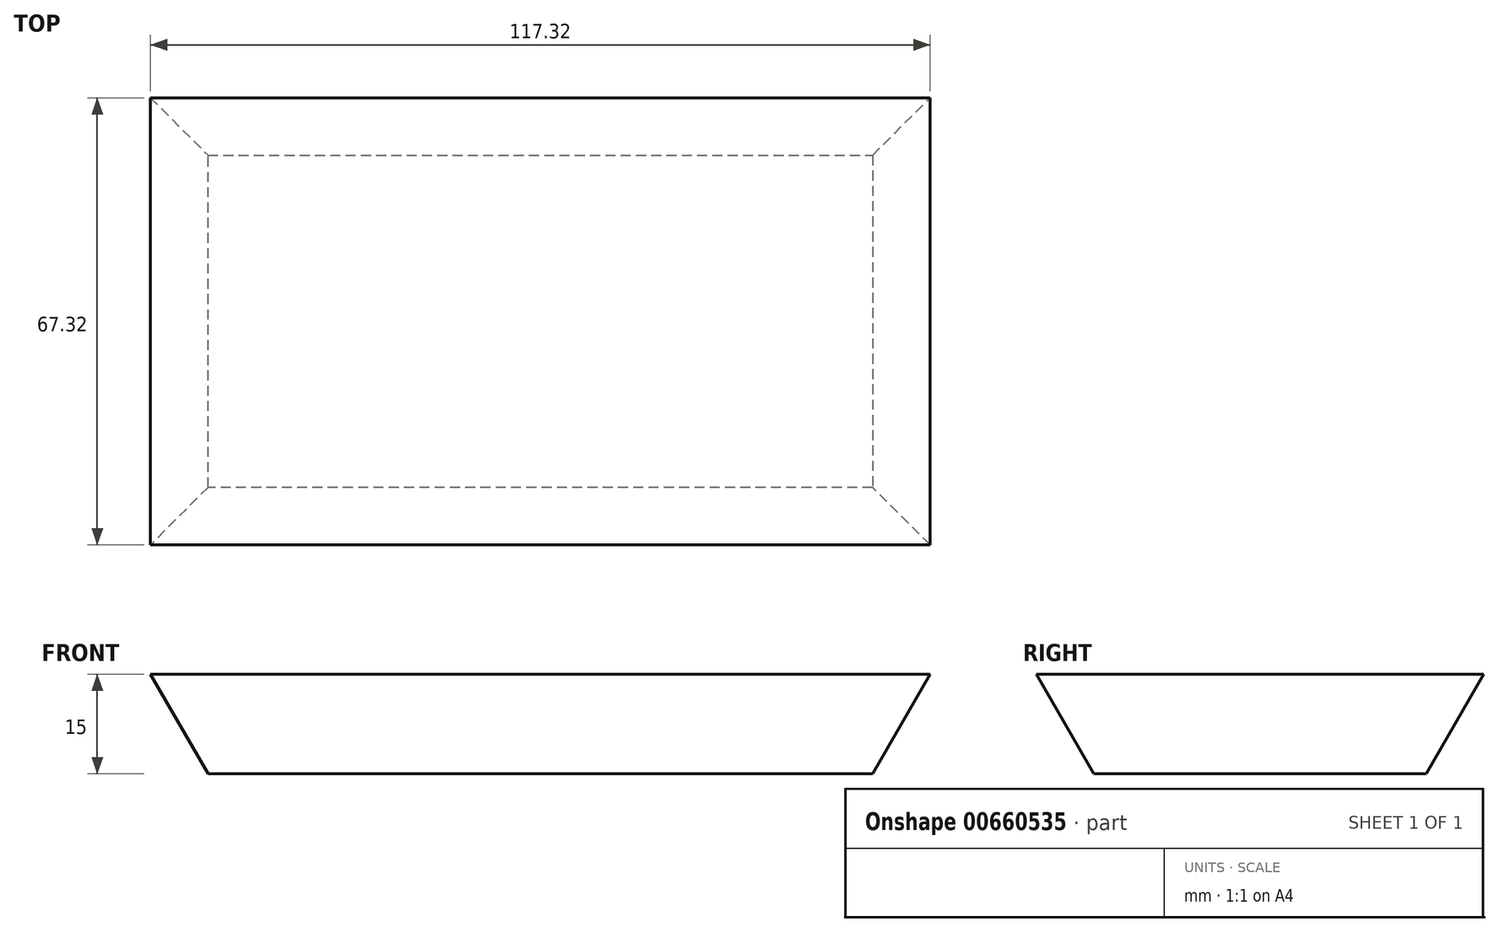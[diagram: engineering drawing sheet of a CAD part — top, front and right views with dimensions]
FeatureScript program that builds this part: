
annotation { "Feature Type Name" : "Feature", "Feature Type Description" : "" }
export const myFeature = defineFeature(function(context is Context, id is Id, definition is map)
    precondition{}
    {
        {
            var Q0;
            Q0=qCreatedBy(makeId("Top.planeOp"),FACE);
            var sketch = newSketch(context, id + "F0", { "sketchPlane" : qUnion([Q0])});
            skLineSegment(sketch, "E0.bottom", {"start": v(0, 0) * mm, "end": v(100, 0) * mm});
            skLineSegment(sketch, "E0.top", {"start": v(0, 50) * mm, "end": v(100, 50) * mm});
            skLineSegment(sketch, "E0.left", {"start": v(0, 0) * mm, "end": v(0, 50) * mm});
            skLineSegment(sketch, "E0.right", {"start": v(100, 0) * mm, "end": v(100, 50) * mm});
            skSolve(sketch);
        }
        {
            var Q0;
            Q0=makeQuery(id+"F0.imprint","IMPRINT",FACE,{"disambiguationData":[TD([[makeQuery(id+"F0.imprint","IMPRINT",EDGE,{"derivedFrom":sQuery(id+"F0.wireOp",EDGE,"E0.bottom")}),1.0]])]});
            extrude(context, id + "F1", {"entities" : qUnion([Q0]), "depth" : 15 * mm, "offsetDistance" : 25 * mm, "hasDraft" : true, "draftAngle" : 30 * degree});
        }
    });
